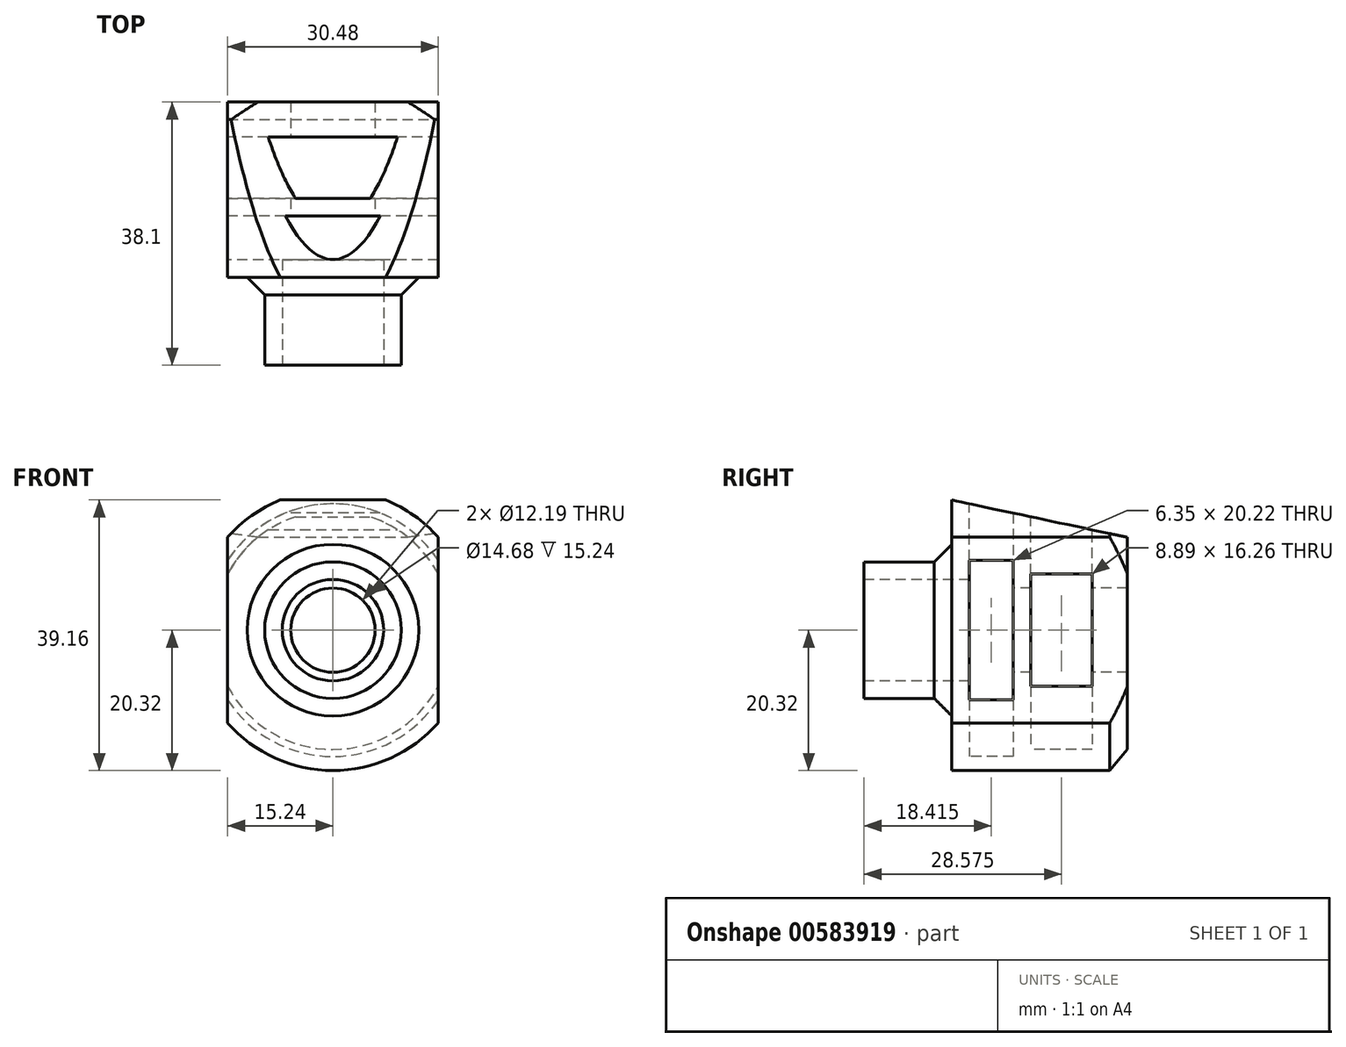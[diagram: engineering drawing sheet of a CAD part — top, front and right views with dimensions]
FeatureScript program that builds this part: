
annotation { "Feature Type Name" : "Feature", "Feature Type Description" : "" }
export const myFeature = defineFeature(function(context is Context, id is Id, definition is map)
    precondition{}
    {
        {
            var Q0;
            Q0=qCreatedBy(makeId("Top.planeOp"),FACE);
            var sketch = newSketch(context, id + "F0", { "sketchPlane" : qUnion([Q0])});
            skLineSegment(sketch, "E0", {"start": v(0, 0) * mm, "end": v(0, 24.31) * mm});
            skLineSegment(sketch, "E1", {"start": v(-7.34, 0) * mm, "end": v(-9.88, 0) * mm});
            skLineSegment(sketch, "E2", {"start": v(-9.88, 0) * mm, "end": v(-9.88, 12.7) * mm});
            skLineSegment(sketch, "E3", {"start": v(-9.88, 12.7) * mm, "end": v(-20.32, 12.7) * mm});
            skLineSegment(sketch, "E4", {"start": v(-20.32, 12.7) * mm, "end": v(-20.32, 35.56) * mm});
            skLineSegment(sketch, "E5", {"start": v(-18.29, 21.6) * mm, "end": v(-18.29, 15.24) * mm});
            skLineSegment(sketch, "E6", {"start": v(-7.34, 15.24) * mm, "end": v(-7.34, 0) * mm});
            skPoint(sketch, "E7.end.orphan", {"position": v(-9.88, 10.2) * mm});
            skPoint(sketch, "E8.end.orphan", {"position": v(-9.88, 16.95) * mm});
            skPoint(sketch, "E9.end.orphan", {"position": v(-9.88, 20.38) * mm});
            skPoint(sketch, "E10.end.orphan", {"position": v(-9.88, 22.48) * mm});
            skLineSegment(sketch, "E11", {"start": v(-17.27, 38.1) * mm, "end": v(-6.1, 38.1) * mm});
            skLineSegment(sketch, "E12", {"start": v(-6.1, 38.1) * mm, "end": v(-6.1, 33.02) * mm});
            skLineSegment(sketch, "E13", {"start": v(-6.1, 33.02) * mm, "end": v(-17.27, 33.02) * mm});
            skLineSegment(sketch, "E14", {"start": v(-18.29, 21.59) * mm, "end": v(-6.1, 21.6) * mm});
            skLineSegment(sketch, "E15", {"start": v(-6.1, 21.6) * mm, "end": v(-6.1, 24.13) * mm});
            skLineSegment(sketch, "E16", {"start": v(-18.29, 15.24) * mm, "end": v(-7.34, 15.24) * mm});
            skPoint(sketch, "E17.end.orphan", {"position": v(-19.84, 24.13) * mm});
            skLineSegment(sketch, "E18", {"start": v(-6.1, 24.13) * mm, "end": v(-17.27, 24.13) * mm});
            skLineSegment(sketch, "E19", {"start": v(-17.27, 24.13) * mm, "end": v(-17.27, 33.02) * mm});
            skPoint(sketch, "E20.orphan", {"position": v(-18.29, 33.02) * mm});
            skLineSegment(sketch, "E21", {"start": v(-20.32, 35.56) * mm, "end": v(-17.27, 38.1) * mm});
            skSolve(sketch);
        }
        {
            var Q0;
            Q0 = qSketchRegion(id + "F0", true);
            var Q1;
            Q1=sQuery(id+"F0.wireOp",EDGE,"E0");
            revolve(context, id + "F1", {"entities" : qUnion([Q0]), "axis" : qUnion([Q1]), "revolveType" : RevolveType.FULL});
        }
        {
            var Q0;
            Q0=makeQuery(id+"F1.opRevolve","SWEPT_FACE",FACE,{"disambiguationData":[OSD([sQuery(id+"F0.wireOp",EDGE,"E11")])]});
            var sketch = newSketch(context, id + "F2", { "sketchPlane" : qUnion([Q0])});
            skLineSegment(sketch, "E22", {"start": v(-15.24, 13.44) * mm, "end": v(-15.24, -13.44) * mm});
            skLineSegment(sketch, "E23", {"start": v(15.24, 13.44) * mm, "end": v(15.24, -13.44) * mm});
            skArc(sketch, "E24", {"start": v(-15.24, 13.44) * mm, "mid": v(-20.32, 0) * mm, "end": v(-15.24, -13.44) * mm});
            skArc(sketch, "E25.trimOffspring", {"start": v(15.24, -13.44) * mm, "mid": v(20.32, 0) * mm, "end": v(15.24, 13.44) * mm});
            skSolve(sketch);
        }
        {
            var Q0;
            Q0 = qSketchRegion(id + "F2", true);
            extrude(context, id + "F3", {"entities" : qUnion([Q0]), "operationType" : NewBodyOperationType.REMOVE, "oppositeDirection" : true, "depth" : 25.4 * mm, "offsetDistance" : 25.4 * mm});
        }
        {
            var Q0;
            Q0=makeQuery(id+"F3.boolean.opBoolean","COPY",FACE,{"derivedFrom":makeQuery(id+"F3.opExtrude","SWEPT_FACE",FACE,{"disambiguationData":[OSD([sQuery(id+"F2.wireOp",EDGE,"E22")])]})});
            var sketch = newSketch(context, id + "F4", { "sketchPlane" : qUnion([Q0])});
            skLineSegment(sketch, "E26", {"start": v(12.7, 13.44) * mm, "end": v(12.7, 18.84) * mm});
            skLineSegment(sketch, "E27", {"start": v(12.7, 18.84) * mm, "end": v(38.1, 13.44) * mm});
            skLineSegment(sketch, "E28", {"start": v(38.1, 13.44) * mm, "end": v(38.1, 25.19) * mm});
            skLineSegment(sketch, "E29", {"start": v(38.1, 25.19) * mm, "end": v(12.7, 25.19) * mm});
            skLineSegment(sketch, "E30", {"start": v(12.7, 25.19) * mm, "end": v(12.7, 18.84) * mm});
            skSolve(sketch);
        }
        {
            var Q0;
            Q0 = qSketchRegion(id + "F4", true);
            extrude(context, id + "F5", {"entities" : qUnion([Q0]), "operationType" : NewBodyOperationType.REMOVE, "endBound" : BoundingType.THROUGH_ALL, "oppositeDirection" : true, "depth" : 25.4 * mm, "offsetDistance" : 25.4 * mm});
        }
        {
            var Q0;
            Q0=makeQuery(id+"F1.opRevolve","SWEPT_EDGE",EDGE,{"disambiguationData":[OSD([sQuery(id+"F0.wireOp",EDGE,"E2"),sQuery(id+"F0.wireOp",EDGE,"E3")])]});
            chamfer(context, id + "F6", {"entities" : qUnion([Q0]), "width" : 2.54 * mm, "tangentPropagation" : true});
        }
    });
